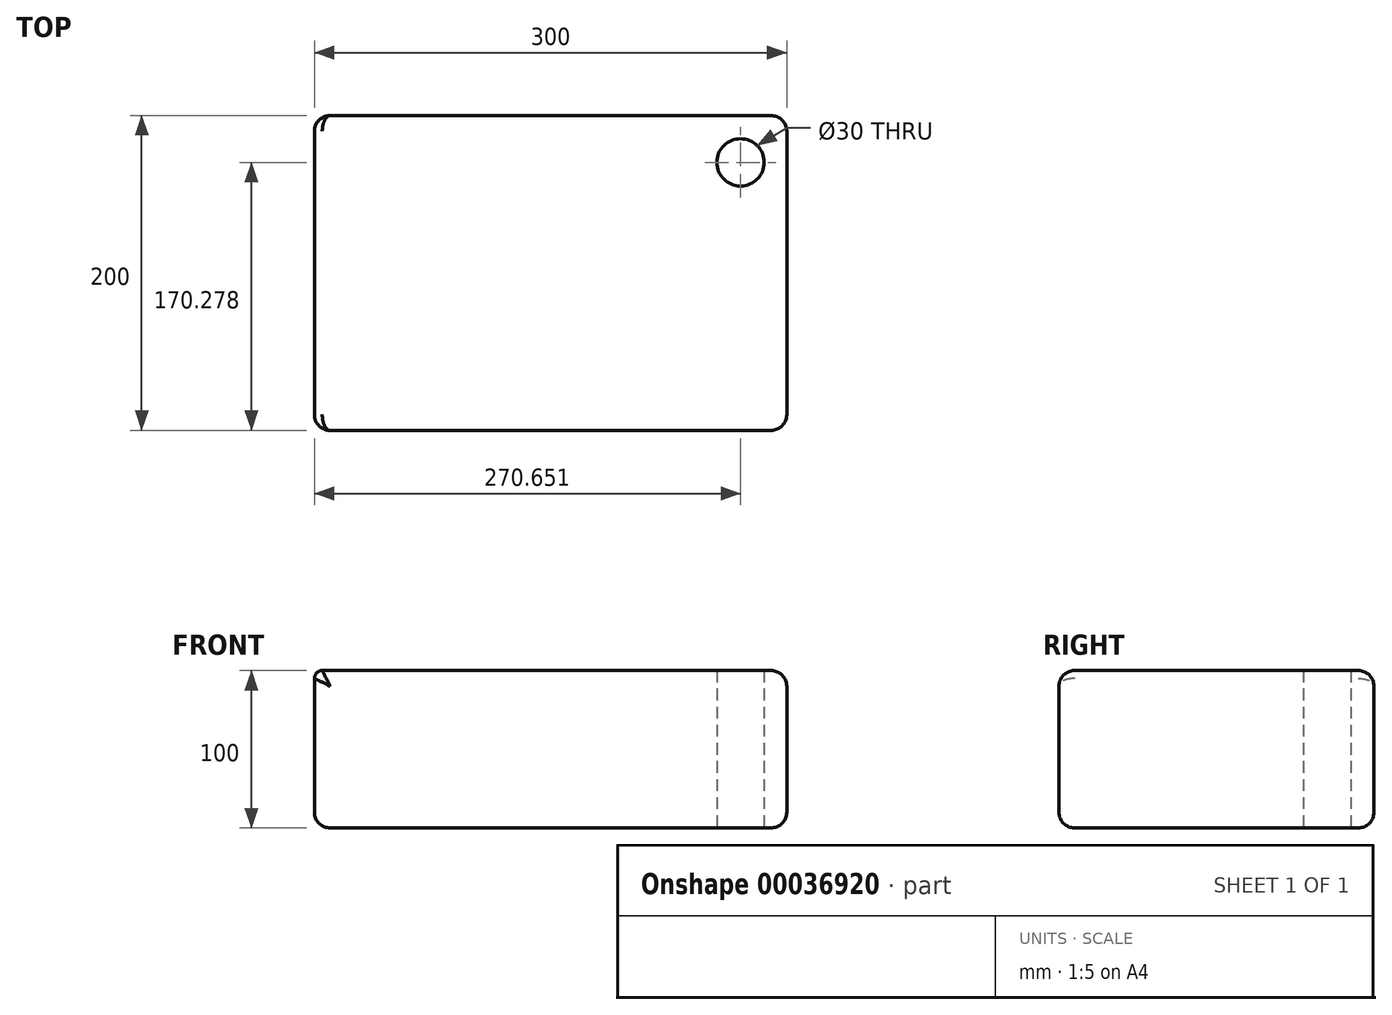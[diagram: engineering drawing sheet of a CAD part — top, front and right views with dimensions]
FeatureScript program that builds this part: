
annotation { "Feature Type Name" : "Feature", "Feature Type Description" : "" }
export const myFeature = defineFeature(function(context is Context, id is Id, definition is map)
    precondition{}
    {
        {
            var Q0;
            Q0=qCreatedBy(makeId("Top.planeOp"),FACE);
            var sketch = newSketch(context, id + "F0", { "sketchPlane" : qUnion([Q0])});
            skLineSegment(sketch, "E0.bottom", {"start": v(-137.23, 100.81) * mm, "end": v(162.77, 100.81) * mm});
            skLineSegment(sketch, "E0.top", {"start": v(-137.23, -99.19) * mm, "end": v(162.77, -99.19) * mm});
            skLineSegment(sketch, "E0.left", {"start": v(-137.23, 100.81) * mm, "end": v(-137.23, -99.19) * mm});
            skLineSegment(sketch, "E0.right", {"start": v(162.77, 100.81) * mm, "end": v(162.77, -99.19) * mm});
            skCircle(sketch, "E1", {"center": v(133.42, 71.09) * mm, "radius": 15 * mm});
            skSolve(sketch);
        }
        {
            var Q0;
            Q0=makeQuery(id+"F0.imprint","IMPRINT",FACE,{"disambiguationData":[TD([[makeQuery(id+"F0.imprint","IMPRINT",EDGE,{"derivedFrom":sQuery(id+"F0.wireOp",EDGE,"E0.bottom")}),-1.0]])]});
            extrude(context, id + "F1", {"entities" : qUnion([Q0]), "depth" : 100 * mm});
        }
        {
            var Q0;
            Q0=makeQuery(id+"F1.opExtrude","CAP_EDGE",EDGE,{"disambiguationData":[OSD([sQuery(id+"F0.wireOp",EDGE,"E0.left")])],"isStart":false});
            fillet(context, id + "F2", {"entities" : qUnion([Q0]), "radius" : 5 * mm, "tangentPropagation" : true, "allowEdgeOverflow" : false});
        }
        {
            var Q0;
            Q0=makeQuery(id+"F1.opExtrude","SWEPT_EDGE",EDGE,{"disambiguationData":[OSD([sQuery(id+"F0.wireOp",EDGE,"E0.bottom"),sQuery(id+"F0.wireOp",EDGE,"E0.left")])]});
            var Q1;
            Q1=makeQuery(id+"F1.opExtrude","CAP_EDGE",EDGE,{"disambiguationData":[OSD([sQuery(id+"F0.wireOp",EDGE,"E0.bottom")])],"isStart":false});
            var Q2;
            Q2=makeQuery(id+"F2.opFillet","BLEND_FACE",FACE,{"disambiguationData":[OSD([sQuery(id+"F0.wireOp",EDGE,"E0.left")])]});
            var Q3;
            Q3=makeQuery(id+"F1.opExtrude","SWEPT_FACE",FACE,{"disambiguationData":[OSD([sQuery(id+"F0.wireOp",EDGE,"E0.right")])]});
            var Q4;
            Q4=makeQuery(id+"F1.opExtrude","SWEPT_EDGE",EDGE,{"disambiguationData":[OSD([sQuery(id+"F0.wireOp",EDGE,"E0.top"),sQuery(id+"F0.wireOp",EDGE,"E0.right")])]});
            var Q5;
            Q5=makeQuery(id+"F1.opExtrude","CAP_EDGE",EDGE,{"disambiguationData":[OSD([sQuery(id+"F0.wireOp",EDGE,"E0.top")])],"isStart":true});
            var Q6;
            Q6=makeQuery(id+"F1.opExtrude","SWEPT_FACE",FACE,{"disambiguationData":[OSD([sQuery(id+"F0.wireOp",EDGE,"E0.bottom")])]});
            var Q7;
            Q7=makeQuery(id+"F1.opExtrude","CAP_EDGE",EDGE,{"disambiguationData":[OSD([sQuery(id+"F0.wireOp",EDGE,"E0.bottom")])],"isStart":true});
            var Q8;
            Q8=makeQuery(id+"F1.opExtrude","CAP_EDGE",EDGE,{"disambiguationData":[OSD([sQuery(id+"F0.wireOp",EDGE,"E0.left")])],"isStart":true});
            var Q9;
            Q9=makeQuery(id+"F1.opExtrude","SWEPT_EDGE",EDGE,{"disambiguationData":[OSD([sQuery(id+"F0.wireOp",EDGE,"E0.top"),sQuery(id+"F0.wireOp",EDGE,"E0.left")])]});
            var Q10;
            Q10=makeQuery(id+"F1.opExtrude","CAP_EDGE",EDGE,{"disambiguationData":[OSD([sQuery(id+"F0.wireOp",EDGE,"E0.right")])],"isStart":true});
            fillet(context, id + "F3", {"entities" : qUnion([Q0, Q1, Q2, Q3, Q4, Q5, Q6, Q7, Q8, Q9, Q10]), "radius" : 10 * mm, "tangentPropagation" : true, "allowEdgeOverflow" : false});
        }
    });
